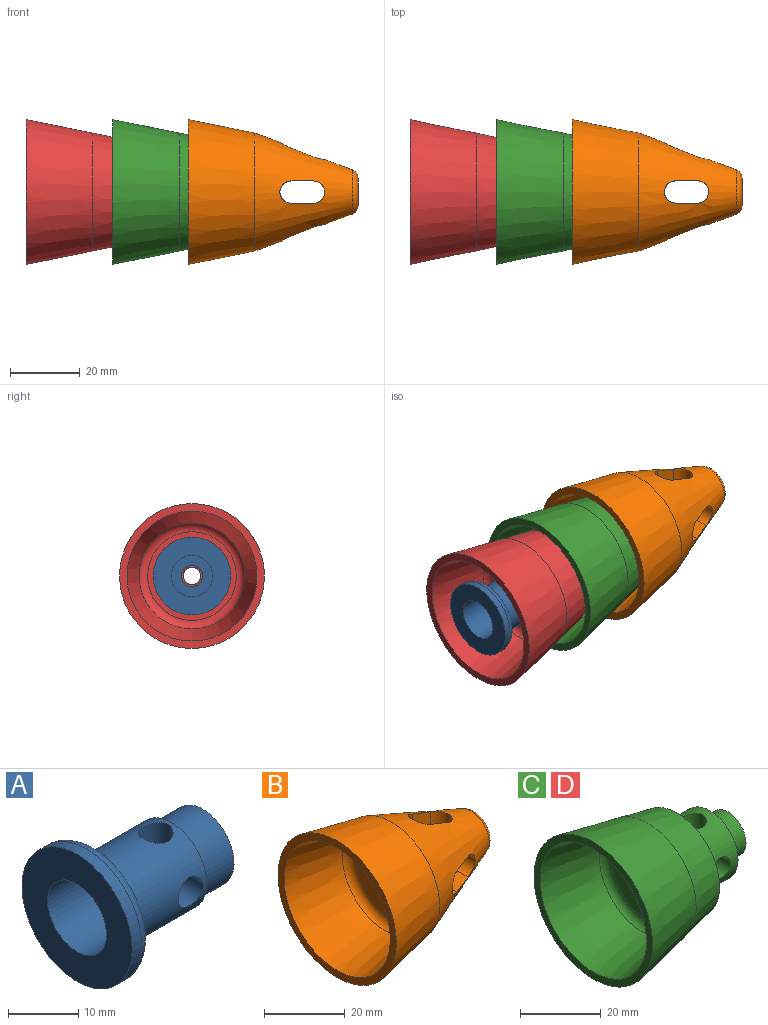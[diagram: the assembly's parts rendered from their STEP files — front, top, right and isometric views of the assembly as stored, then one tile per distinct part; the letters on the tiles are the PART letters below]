
ASSEMBLY  parts=4 mates=4
PART A: 17 faces, bbox 25.4x24.1x24.1 mm
  f0: cylinder r=3.05mm len=6.1mm, axis (-1,0,0), area 20.5mm2, adj f11,f13,f14,f15,f16
  f1: plane 12.59x12.59mm, normal (1,0,0), area 95.3mm2, adj f2,f12
  f2: cylinder r=6.29mm len=12.59mm, axis (-1,0,0), area 251.1mm2, adj f1,f3
  f3: plane 14.28x14.28mm, normal (1,0,0), area 35.8mm2, adj f2,f4
  f4: cylinder r=7.14mm len=14.28mm, axis (-1,0,0), area 519.3mm2, adj f3,f5,f13,f14,f15,f16
  f5: torus R=9.05mm, axis (-1,0,0), area 147.3mm2, adj f4,f6
  f6: plane 18.44x18.44mm, normal (1,0,0), area 9.9mm2, adj f5,f7
  f7: torus R=9.22mm, axis (-1,0,0), area 196.2mm2, adj f6,f8
  f8: cylinder r=11.13mm len=22.25mm, axis (-1,0,0), area 132mm2, adj f7,f9
  f9: plane 22.25x22.25mm, normal (-1,0,0), area 277.9mm2, adj f8,f10
  f10: cylinder r=5.94mm len=12.7mm, axis (-1,0,0), area 474.3mm2, adj f9,f11
  f11: plane 11.89x11.89mm, normal (-1,0,0), area 81.8mm2, adj f0,f10
  f12: cylinder r=3.05mm len=8.26mm, axis (-1,0,0), area 142.1mm2, adj f1,f13,f14,f15,f16
  f13: cylinder r=2.5mm len=5mm, axis (0,0,1), area 67.7mm2, adj f0,f4,f12,f15,f16
  f14: cylinder r=2.5mm len=5mm, axis (0,0,1), area 67.7mm2, adj f0,f4,f12,f15,f16
  f15: cylinder r=2.5mm len=5mm, axis (0,-1,0), area 67.7mm2, adj f0,f4,f12,f13,f14
  f16: cylinder r=2.5mm len=5mm, axis (0,-1,0), area 67.7mm2, adj f0,f4,f12,f13,f14
PART B: 28 faces, bbox 48.6x41.6x41.6 mm
  f0: cylinder r=2.48mm len=10.06mm, axis (-1,0,0), area 151.6mm2, adj f3,f4,f16,f23,f26
  f1: cone r=16.89mm half-angle=20.7deg, axis (-1,0,0), area 1860.7mm2, adj f3,f4,f5,f6,f7,f8,f9,f17
  f2: cylinder r=2.48mm len=4.97mm, axis (-1,0,0), area 16.6mm2, adj f6,f7,f15,f22,f24
  f3: cylinder r=3.17mm len=8.29mm, axis (0,0,1), area 69.7mm2, adj f0,f1,f5,f8,f23,f26
  f4: cylinder r=3.17mm len=8.29mm, axis (0,0,1), area 69.7mm2, adj f0,f1,f18,f19,f23,f26
  f5: plane 9.44x6.42mm, normal (0,-1,0), area 51.6mm2, adj f1,f3,f6,f25
  f6: cylinder r=3.17mm len=12.27mm, axis (0,0,1), area 109mm2, adj f1,f2,f5,f8,f21,f22,f24,f25
  f7: cylinder r=3.17mm len=12.27mm, axis (0,0,1), area 109mm2, adj f1,f2,f18,f19,f20,f22,f24,f27
  f8: plane 9.44x6.42mm, normal (0,1,0), area 51.6mm2, adj f1,f3,f6,f21
  f9: cone r=20.75mm half-angle=11.4deg, axis (-1,0,0), area 2297.9mm2, adj f1,f10
  f10: plane 41.49x41.49mm, normal (-1,0,0), area 261.1mm2, adj f9,f11
  f11: cone r=15.19mm half-angle=11.4deg, axis (-1,0,0), area 1845.1mm2, adj f10,f12
  f12: torus R=12.7mm, axis (-1,0,0), area 309.9mm2, adj f11,f13
  f13: plane 25.4x25.4mm, normal (-1,0,0), area 395.7mm2, adj f12,f14
  f14: cylinder r=5.94mm len=11.89mm, axis (-1,0,0), area 237.1mm2, adj f13,f15
  f15: plane 11.89x11.89mm, normal (-1,0,0), area 91.6mm2, adj f2,f14
  f16: plane 7.96x7.96mm, normal (1,0,0), area 30.4mm2, adj f0,f17
  f17: torus R=3.98mm, axis (-1,0,0), area 103mm2, adj f1,f16
  f18: plane 9.44x6.42mm, normal (0,-1,0), area 51.6mm2, adj f1,f4,f7,f27
  f19: plane 9.44x6.42mm, normal (0,1,0), area 51.6mm2, adj f1,f4,f7,f20
  f20: plane 9.5x6.58mm, normal (0,0,-1), area 53mm2, adj f1,f7,f19,f22,f23
  f21: plane 9.5x6.58mm, normal (0,0,1), area 53mm2, adj f1,f6,f8,f22,f23
  f22: cylinder r=3.17mm len=12.55mm, axis (0,1,0), area 110.7mm2, adj f1,f2,f6,f7,f20,f21
  f23: cylinder r=3.17mm len=8.29mm, axis (0,1,0), area 69.7mm2, adj f0,f1,f3,f4,f20,f21
  f24: cylinder r=3.17mm len=12.55mm, axis (0,1,0), area 110.7mm2, adj f1,f2,f6,f7,f25,f27
  f25: plane 9.5x6.58mm, normal (0,0,1), area 53mm2, adj f1,f5,f6,f24,f26
  f26: cylinder r=3.17mm len=8.29mm, axis (0,1,0), area 69.7mm2, adj f0,f1,f3,f4,f25,f27
  f27: plane 9.5x6.58mm, normal (0,0,-1), area 53mm2, adj f1,f7,f18,f24,f26
PART C: 19 faces, bbox 47.1x41.5x41.5 mm
  f0: cylinder r=2.48mm len=9.42mm, axis (-1,0,0), area 141.7mm2, adj f3,f4,f13,f17,f18
  f1: cylinder r=2.48mm len=4.97mm, axis (-1,0,0), area 4.4mm2, adj f3,f4,f12,f17,f18
  f2: cylinder r=9.86mm len=19.72mm, axis (-1,0,0), area 574.9mm2, adj f3,f4,f15,f16,f17,f18
  f3: cylinder r=3.17mm len=8.1mm, axis (0,0,1), area 141.2mm2, adj f0,f1,f2,f17,f18
  f4: cylinder r=3.17mm len=8.1mm, axis (0,0,1), area 141.2mm2, adj f0,f1,f2,f17,f18
  f5: cone r=16.89mm half-angle=11.6deg, axis (-1,0,0), area 1049.1mm2, adj f6,f16
  f6: cone r=20.75mm half-angle=11.4deg, axis (-1,0,0), area 2297.9mm2, adj f5,f7
  f7: plane 41.49x41.49mm, normal (-1,0,0), area 262.3mm2, adj f6,f8
  f8: cone r=15.14mm half-angle=11.4deg, axis (-1,0,0), area 1864.6mm2, adj f7,f9
  f9: torus R=12.7mm, axis (-1,0,0), area 289.1mm2, adj f8,f10
  f10: plane 25.4x25.4mm, normal (-1,0,0), area 395.7mm2, adj f9,f11
  f11: cylinder r=5.94mm len=12.7mm, axis (-1,0,0), area 474.3mm2, adj f10,f12
  f12: plane 11.89x11.89mm, normal (-1,0,0), area 91.6mm2, adj f1,f11
  f13: plane 12.59x12.59mm, normal (1,0,0), area 105.1mm2, adj f0,f14
  f14: cylinder r=6.29mm len=12.59mm, axis (-1,0,0), area 251.1mm2, adj f13,f15
  f15: plane 19.72x19.72mm, normal (1,0,0), area 180.9mm2, adj f2,f14
  f16: plane 29.55x29.55mm, normal (1,0,0), area 380.2mm2, adj f2,f5
  f17: cylinder r=3.17mm len=8.1mm, axis (0,1,0), area 141.2mm2, adj f0,f1,f2,f3,f4
  f18: cylinder r=3.17mm len=8.1mm, axis (0,1,0), area 141.2mm2, adj f0,f1,f2,f3,f4
PART D: same geometry as C
PLACE A t=(2.68,2.87,1.45)mm
PLACE B t=(68.27,2.87,1.45)mm
PLACE C t=(46.59,2.87,1.45)mm
PLACE D t=(21.73,2.87,1.45)mm
MATE slider C.f0 <-> B.f0  axis (-1,0,0) through (71.45,2.87,1.45)mm
MATE slider C.f0 <-> D.f0  axis (-1,0,0) through (46.59,2.87,1.45)mm
MATE slider C.f0 <-> D.f0  axis (-1,0,0) through (59.29,2.87,1.45)mm
MATE slider A.f0 <-> D.f0  axis (1,0,0) through (21.73,2.87,1.45)mm
